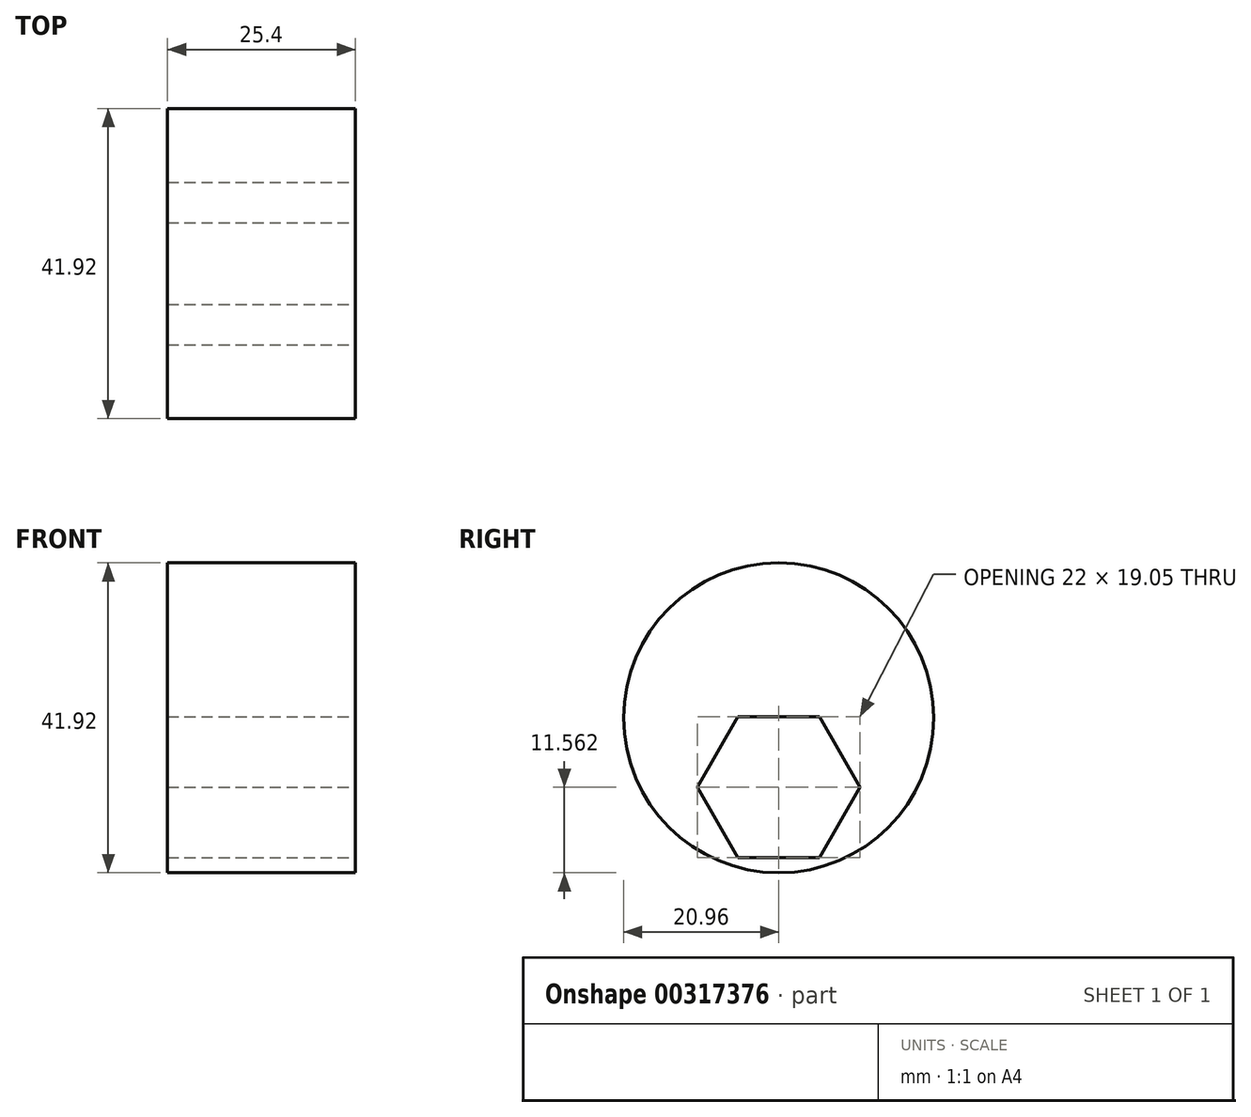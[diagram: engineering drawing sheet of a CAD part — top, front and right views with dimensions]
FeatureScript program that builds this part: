
annotation { "Feature Type Name" : "Feature", "Feature Type Description" : "" }
export const myFeature = defineFeature(function(context is Context, id is Id, definition is map)
    precondition{}
    {
        {
            var Q0;
            Q0=qCreatedBy(makeId("Right.planeOp"),FACE);
            var sketch = newSketch(context, id + "F0", { "sketchPlane" : qUnion([Q0])});
            skCircle(sketch, "E0", {"center": v(0, 0) * mm, "radius": 20.96 * mm});
            skSolve(sketch);
        }
        {
            var Q0;
            Q0=makeQuery(id+"F0.imprint","IMPRINT",FACE,{"disambiguationData":[TD([[makeQuery(id+"F0.imprint","IMPRINT",EDGE,{"derivedFrom":sQuery(id+"F0.wireOp",EDGE,"E0")}),1.0]])]});
            extrude(context, id + "F1", {"entities" : qUnion([Q0]), "depth" : 25.4 * mm});
        }
        {
            var Q0;
            Q0=makeQuery(id+"F1.opExtrude","CAP_FACE",FACE,{"disambiguationData":[OSD([sQuery(id+"F0.wireOp",EDGE,"E0")])],"isStart":false});
            var sketch = newSketch(context, id + "F2", { "sketchPlane" : qUnion([Q0])});
            skLineSegment(sketch, "E1", {"start": v(0, 0) * mm, "end": v(0, -9.4) * mm});
            skLineSegment(sketch, "E2", {"start": v(0, -9.4) * mm, "end": v(0, -18.92) * mm});
            skCircle(sketch, "E3.cCircle", {"center": v(0, -9.4) * mm, "radius": 9.53 * mm, "construction": true});
            skLineSegment(sketch, "E3.0", {"start": v(5.5, -18.92) * mm, "end": v(-5.5, -18.92) * mm});
            skLineSegment(sketch, "E3.1", {"start": v(-5.5, -18.92) * mm, "end": v(-11, -9.4) * mm});
            skLineSegment(sketch, "E3.2", {"start": v(-11, -9.4) * mm, "end": v(-5.5, 0.13) * mm});
            skLineSegment(sketch, "E3.3", {"start": v(-5.5, 0.13) * mm, "end": v(5.5, 0.13) * mm});
            skLineSegment(sketch, "E3.4", {"start": v(5.5, 0.13) * mm, "end": v(11, -9.4) * mm});
            skLineSegment(sketch, "E3.5", {"start": v(11, -9.4) * mm, "end": v(5.5, -18.92) * mm});
            skPoint(sketch, "E3.0.midPoint", {"position": v(0, -18.92) * mm});
            skSolve(sketch);
        }
        {
            var Q0;
            {var subQ0=sQuery(id+"F2.wireOp",EDGE,"E3.1");Q0=makeQuery(id+"F2.imprint","IMPRINT",FACE,{"disambiguationData":[TD([[makeQuery(id+"F2.imprint","IMPRINT",EDGE,{"derivedFrom":subQ0}),-1.0]])]});}
            extrude(context, id + "F3", {"entities" : qUnion([Q0]), "operationType" : NewBodyOperationType.REMOVE, "oppositeDirection" : true, "depth" : 25.4 * mm});
        }
    });
